# Revit family: 303_R402HX_
name_source: partatom
category: Pipe Accessories
revit_build: Autodesk Revit 2018 (Build: 20170223_1515(x64)
units: mm (PartAtom-declared; Revit-internal decimal feet)

## family parameters
Always vertical = Yes
Cut with Voids When Loaded = No
Part Type = Valve - Breaks Into
Round Connector Dimension = Use Diameter
Shared = No
Work Plane-Based = No

## types (2) — shared parameters
CAT0 = Yes
CAT1 = No
Description = Straight valve with thermostatic option
J2 = 2 mm  [stored 0.00656168 ft]
L2D_Min = 3048 mm  [stored 10 ft]
M1 = 17 mm  [stored 0.0557743 ft]
M2 = 15 mm  [stored 0.0492126 ft]
M3 = 11 mm
Manufacturer = Giacomini
QmdConnectorList = 301;D;302;D1
URL = http://www.giacomini.com
magiPartTypeId = 303
magiProductFamilyId = R402HX*
zero-valued in all types: MC_Default_elevation

## per-type parameters (varying)
- R402HX003: B1=9 mm  [stored 0.0295276 ft]; CenSd_K2_6=12 mm  [stored 0.0393701 ft]; CenSd_W2_6=13 mm; D=15 mm; D1=15 mm; H2=22 mm  [stored 0.0721785 ft]; K2=14 mm  [stored 0.0459318 ft]; K3=11 mm; K4=18 mm  [stored 0.0590551 ft]; L2=11 mm; L2D=71 mm; L4=8 mm  [stored 0.0262467 ft]; L5=22 mm  [stored 0.0721785 ft]; L6=11 mm; LC=62 mm  [stored 0.203412 ft]; LC1=36 mm; LC2=59 mm; LX=34 mm; R1=11 mm; W2=15 mm  [stored 0.0492126 ft]; W2D=15 mm  [stored 0.0492126 ft]; W3=12 mm  [stored 0.0393701 ft]; W4=9 mm  [stored 0.0295276 ft]; W5=13 mm; W6=7 mm  [stored 0.0229659 ft]; X1=15 mm  [stored 0.0492126 ft]
- R402HX004: B1=11 mm; CenSd_K2_6=14 mm  [stored 0.0459318 ft]; CenSd_W2_6=16 mm; D=20 mm; D1=20 mm; H2=26 mm; K2=16 mm; K3=13 mm; K4=20 mm  [stored 0.0656168 ft]; L2=12 mm  [stored 0.0393701 ft]; L2D=81 mm; L4=9 mm  [stored 0.0295276 ft]; L5=25 mm  [stored 0.082021 ft]; L6=13 mm; LC=70 mm; LC1=41 mm; LC2=68 mm; LX=40 mm; R1=13 mm; W2=19 mm; W2D=20 mm  [stored 0.0656168 ft]; W3=15 mm  [stored 0.0492126 ft]; W4=11 mm; W5=16 mm; W6=9 mm  [stored 0.0295276 ft]; X1=16 mm

note: column(s) folded — value = type name in every type: magiProductCode, magiProductId

note: [stored X ft] marks values corroborated as IEEE doubles in the binary element streams (Revit-internal decimal feet)
